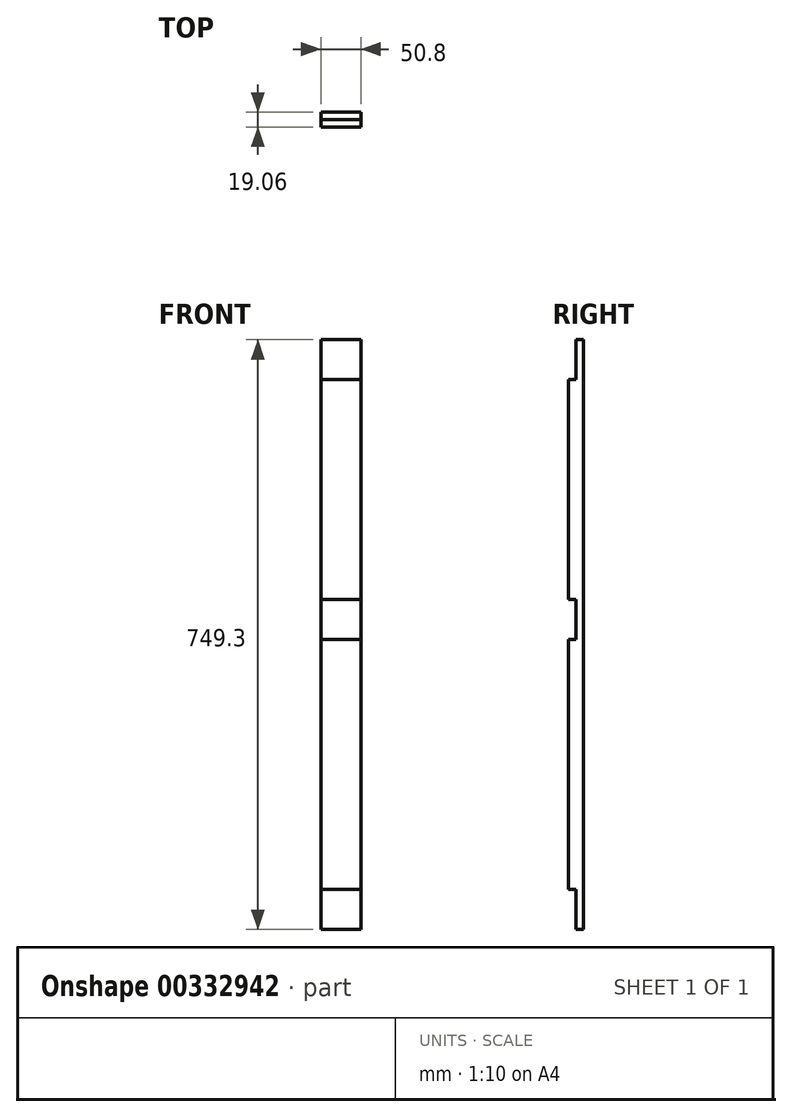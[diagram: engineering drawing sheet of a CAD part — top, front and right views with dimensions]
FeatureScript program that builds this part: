
annotation { "Feature Type Name" : "Feature", "Feature Type Description" : "" }
export const myFeature = defineFeature(function(context is Context, id is Id, definition is map)
    precondition{}
    {
        {
            var Q0;
            Q0=qCreatedBy(makeId("Top.planeOp"),FACE);
            var sketch = newSketch(context, id + "F0", { "sketchPlane" : qUnion([Q0])});
            skLineSegment(sketch, "E0.bottom", {"start": v(25.4, 9.53) * mm, "end": v(-25.4, 9.53) * mm});
            skLineSegment(sketch, "E0.top", {"start": v(25.4, -9.53) * mm, "end": v(-25.4, -9.53) * mm});
            skLineSegment(sketch, "E0.left", {"start": v(25.4, 9.53) * mm, "end": v(25.4, -9.52) * mm});
            skLineSegment(sketch, "E0.right", {"start": v(-25.4, 9.53) * mm, "end": v(-25.4, -9.53) * mm});
            skPoint(sketch, "E0.middle", {"position": v(0, 0) * mm});
            skSolve(sketch);
        }
        {
            var Q0;
            Q0=makeQuery(id+"F0.imprint","IMPRINT",FACE,{"disambiguationData":[TD([[makeQuery(id+"F0.imprint","IMPRINT",EDGE,{"derivedFrom":sQuery(id+"F0.wireOp",EDGE,"E0.bottom")}),1.0]])]});
            extrude(context, id + "F1", {"entities" : qUnion([Q0]), "depth" : 749.3 * mm});
        }
        {
            var Q0;
            Q0=qCreatedBy(makeId("Front.planeOp"),FACE);
            var sketch = newSketch(context, id + "F2", { "sketchPlane" : qUnion([Q0])});
            skLineSegment(sketch, "E1.bottom", {"start": v(-38.77, 0) * mm, "end": v(83.66, 0) * mm});
            skLineSegment(sketch, "E1.top", {"start": v(-38.77, 50.8) * mm, "end": v(83.66, 50.8) * mm});
            skLineSegment(sketch, "E1.left", {"start": v(-38.77, 0) * mm, "end": v(-38.77, 50.8) * mm});
            skLineSegment(sketch, "E1.right", {"start": v(83.66, 0) * mm, "end": v(83.66, 50.8) * mm});
            skLineSegment(sketch, "E2.bottom", {"start": v(-44.21, 368.3) * mm, "end": v(49.65, 368.3) * mm});
            skLineSegment(sketch, "E2.top", {"start": v(-44.21, 419.1) * mm, "end": v(49.65, 419.1) * mm});
            skLineSegment(sketch, "E2.left", {"start": v(-44.21, 368.3) * mm, "end": v(-44.21, 419.1) * mm});
            skLineSegment(sketch, "E2.right", {"start": v(49.65, 368.3) * mm, "end": v(49.65, 419.1) * mm});
            skLineSegment(sketch, "E3.bottom", {"start": v(-210.36, 698.5) * mm, "end": v(132.8, 698.5) * mm});
            skLineSegment(sketch, "E3.top", {"start": v(-210.36, 749.3) * mm, "end": v(132.8, 749.3) * mm});
            skLineSegment(sketch, "E3.left", {"start": v(-210.36, 698.5) * mm, "end": v(-210.36, 749.3) * mm});
            skLineSegment(sketch, "E3.right", {"start": v(132.8, 698.5) * mm, "end": v(132.8, 749.3) * mm});
            skSolve(sketch);
        }
        {
            var Q0;
            Q0=qSketchRegion(id+"F2",true);
            extrude(context, id + "F3", {"entities" : qUnion([Q0]), "operationType" : NewBodyOperationType.REMOVE, "depth" : 25.4 * mm});
        }
    });
